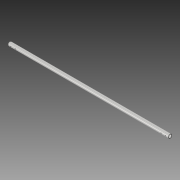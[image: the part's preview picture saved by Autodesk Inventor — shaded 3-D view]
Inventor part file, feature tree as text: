
AUTODESK INVENTOR PART (.ipt)
format: ipt  version: 2018 (Build 220112000, 112)  size: 103,936 bytes
history: native  units: in
note: dims shown in document units (in); Inventor stores cm internally (conversion verified against a paired STEP export)
features: mirror x1
ambient origin geometry x8: Origin, YZ Plane, XZ Plane, XY Plane, X Axis, Y Axis, Z Axis, Center Point
bodies: Solid1 (feature_tree)
feature tree (1):
  mirror  "Mirror1"
